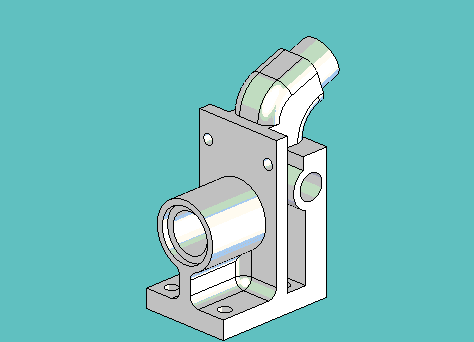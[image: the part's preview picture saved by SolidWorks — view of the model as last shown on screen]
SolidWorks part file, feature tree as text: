
SOLIDWORKS PART (.sldprt)
format: sldprt  version: not decoded by parser v0  size: 2,849,792 bytes
history: native  units: mm
features: sketch x20, boolean_combine x9, cut_extrude x9, extrude x8, fillet x3, material x1, plane x1, revolve x1, chamfer x1, sweep x1 (+11 scaffold rows collapsed)
feature tree (65):
  scaffold x11  (default folders/planes/origin — collapsed)
  material  "Material <not specified>"
  sketch  "Sketch1"  dims[D1=4.7498mm D2=11.43mm D3=11.43mm D4=30.9626mm]
  extrude  "Extrude1"  Depth=41.275mm
  sketch  "Sketch5"  dims[D1=5.6515mm D2=5.6515mm D3=14.097mm]
  extrude  "Extrude7"  Depth=4.7752mm
  boolean_combine  "Combine4"
  sketch  "Sketch6"  dims[D2=7.0358mm D1=20.6502mm]
  extrude  "Extrude8"  Depth=38.1mm
  plane  "Plane1"
  boolean_combine  "Combine5"
  sketch  "Sketch7"  dims[D1=10.16mm]
  extrude  "Extrude10"  Depth=21.6916mm
  boolean_combine  "Combine6"
  sketch  "Sketch8"  dims[D1=6.604mm D2=4.7752mm]
  extrude  "Extrude11"  [1 undecoded]
  boolean_combine  "Combine7"
  sketch  "Sketch9"  dims[c1.D3=6.5278mm c1.D1=28.956mm c1.D2=4.7625mm c2.D1=27.1272mm]
  extrude  "Extrude12"  Depth=38.1mm
  boolean_combine  "Combine8"
  sketch  "Sketch11"  dims[c1.D1=0.381mm c1.D2=3.175mm c2.D1=3.175mm c2.D3=0.254mm c2.D4=7.62mm c2.D2=0.381mm]
  revolve  "Revolve2"  Angle=360deg
  boolean_combine  "Combine11"
  sketch  "Sketch12"  dims[c1.D1=3.175mm c1.D2=3.175mm c1.D3=3.175mm c1.D7=3.175mm c1.D4=9.525mm c1.D5=7.9248mm c1.D6=7.9248mm c2.D7=26.9748mm c2.D8=26.9748mm c2.D4=26.9875mm c2.D3=7.9248mm c2.D6=9.525mm c2.D5=7.9248mm c3.D8=7.9248mm c3.D9=9.525mm c4.D8=7.9248mm]
  extrude  "Extrude14"  Depth=12.7mm
  boolean_combine  "Combine12"
  chamfer  "Chamfer1"  Distance=0.889mm Angle=15deg
  sketch  "Sketch21"  dims[D1=3.175mm D2=15.875mm]
  cut_extrude  "Cut-Extrude6"  [1 undecoded]
  sketch  "Sketch24"  dims[c1.D2=2.032mm c1.D3=~2.38125mm c1.D4=~2.38125mm c1.D5=3.175mm c1.D1=4.7625mm c2.D3=3.175mm c2.D4=1.5875mm c2.D5=1.5875mm c2.D1=0.0mm]
  cut_extrude  "Cut-Extrude9"  [1 undecoded]
  fillet  "Fillet1"  Radius=2.38125mm
  sketch  "Sketch25"  dims[c1.D2=6.5278mm c1.D1=3.175mm c2.D2=22.225mm c2.D3=6.35mm c3.D2=1.778mm c3.D4=3.175mm c3.D5=7.9375mm c4.D4=31.75mm]
  cut_extrude  "Cut-Extrude10"  Depth=5.55625mm
  sketch  "Sketch26"  dims[D1=0.0mm]
  cut_extrude  "Cut-Extrude11"  Depth=5.55625mm
  sketch  "Sketch27"  dims[D3=2.7051mm D5=2.7051mm D1=34.925mm D2=8.89mm D4=8.89mm]
  cut_extrude  "Cut-Extrude12"  [1 undecoded]
  sketch  "Sketch29"  dims[D1=0.0mm]
  cut_extrude  "Cut-Extrude14"  Depth=6.35mm
  sketch  "Sketch30"
  sketch  "Sketch31"  dims[c1.D1=~20.20113mm c2.D1=70.0deg c2.D2=12.7mm c2.D3=6.35mm c2.D4=4.953mm c2.D5=4.953mm]
  sweep  "Sweep1"
  sketch  "Sketch32"  dims[c1.D1=9.525mm c1.D4=5.08mm c1.D3=6.35mm c2.D1=~7.666823mm c3.D1=54.0deg c3.D2=~15.09935mm c4.D2=42.0deg c4.D1=5.08mm c5.D2=5.08mm c5.D3=6.35mm c5.D1=~5.87502mm c6.D2=~5.87502mm]
  extrude  "Extrude15"  [1 undecoded]
  boolean_combine  "Combine13"
  boolean_combine  "Combine14"
  sketch  "Sketch33"  dims[D1=7.1628mm]
  cut_extrude  "Cut-Extrude15"  Depth=6.35mm
  sketch  "Sketch34"  dims[D2=10.414mm D3=3.175mm D4=3.175mm D1=0.0mm]
  cut_extrude  "Cut-Extrude16"  Depth=6.35mm
  fillet  "Fillet2"  Radius=3.175mm
  fillet  "Fillet3"  Radius=0.79375mm
  sketch  "Sketch37"  dims[D1=13.5128mm]
  cut_extrude  "Cut-Extrude18"  Depth=1.5875mm
decode coverage: 36 of 52 modeling features carry decoded parameters
note: ~ marks probable driven/reference dimensions
note: 5 parameter values undecoded
summary: no parameter record found for 5 features
note: suppression state not decoded; provenance and decode notes live in map.json
